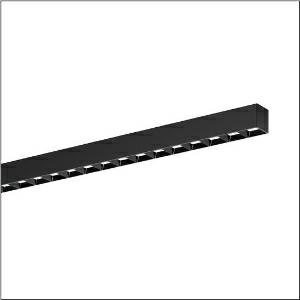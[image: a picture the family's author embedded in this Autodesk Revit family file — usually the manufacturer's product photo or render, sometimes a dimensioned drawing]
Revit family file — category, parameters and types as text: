
# Revit family: silica_r__21_51mx21tctab_539a
name_source: partatom
category: Lighting Fixtures
units: mm (PartAtom-declared; Revit-internal decimal feet)

## family parameters
Cut with Voids When Loaded = No
Host = Face
Light Source = No
Part Type = Normal
Room Calculation Point = No
Round Connector Dimension = Use Diameter
Shared = No

## types (1)
- --- (1 x LED, 9300 lm, 80.5 W, 6500K)
    Apparent Load = 81 VA
    CIE Flux Codes = 85 99 100 100 100
    Color Rendering = 80
    Color Temperature = 6500K
    Default Elevation = 1800 mm
    Description = Silica® 21, office luminaire, primary light control with darklight reflector, of PMMA, black, CAT 2 (L<= 3000cd/m²), light emission: direct distribution, primary light characteristic: symmetric, installation type: surface-mounted, LED, rated luminous flux: 9.300lm, luminous efficacy: 110lm/W, light colour: 8tw, colour temperature: 2700..6500K, control gear: DALI DT8, with terminal, 3+2-pole, max. 2.5mm², mains connection: 220..240V, AC, 50/60Hz, rated input power: 84.6W, luminaire housing, of aluminium, matt jet black (RAL 9005), length: 3.004mm, width: 53mm, height: 53mm, protection rating (complete): IP20, insulation class (complete): insulation class I (protective earthing), certification: CE, permissible operating ambient temperature: 0..+35°C, standard: EN 50419, packaging unit: 1 piece
    Height = 53 mm
    Lamp = 1 x LED
    Lamp Light Flux = 9300 lm
    Lamp Power = 80.5 W
    Lamp count = 1
    Length = 3004 mm
    Luminous efficacy = 116 lm/W
    Manufacturer = Siteco
    ModVariant = No
    Model = 51MX21TCTAB
    Mounting Place = Ceiling
    Mounting Type = Surface mounted
    Number of Poles = 1
    OnlyDefault = Yes
    Power Factor = 1
    Product Name = Silica® 21
    Product group = office luminaire | ceiling mounted
    ProductGroupID = 302
    Protection Class = Protection class I
    Protection Degree = IP 20
    RLX_Detail_Level = 1
    RLX_Emergency_Light_Flux = 0 lm
    RLX_Emergency_Type = 0
    RLX_Emergency_Type_DB = No
    RlxData = <blob elided: 60693 chars, md5=e1c714c1>
    Socket = socket
    Standby Power = 0 W
    System Light Flux = 9300 lm
    System Power = 81 W
    Type Comments = individual setting
    Type Image = l_1335908.jpg
    URL = http://relux.com
    VarID = @adj_140058
    Voltage = 0 V
    Weight = 0.00 kg
    Width = 53 mm

## geometry (parser evidence)
native form markers: Blend x4, Sweep x12
no freeform markers — native parametric forms only
